# Revit family: Waste_Bin-Sotare-Magnuson_Group-
name_source: partatom
category: Furniture
revit_build: Autodesk Revit 2014 (Build: 20130308_1515(x64)
units: mm (PartAtom-declared; Revit-internal decimal feet)

## types (4) — shared parameters
Color/ Finish = Dark Anthracite. Anodized Silver. Luner White. Bronze Metallic.
Depth = 18"
Height = 33 3/4"
Manufacturer = Magnuson Group
Powder Coat Paint = MAG - Dark Anthracite
Type Comments = SOTARE
URL = www.magnusongroup.com
Width = 18"

## per-type parameters (varying)
| type | Center | Cost | Description | Full Body | Full Lid_Circle/Paper | Full Lid_Waste | Glide Finish | Left | Left Feet | Right | Right Feet |
| SO1809L-RIGHT | Yes | 1095 $ | Right side quarter elliptical shaped waste basket with internal rigid liner and removable wire bag ring. Includes one standard icon and adjustable glides. Capacity 14 gallons. | No | No | No | <By Category> | No | No | Yes | Yes |
| SO1809L-LEFT | Yes | 1095 $ | Left side quarter elliptical shaped waste receptacle with internal rigid liner and removable wire bag ring. Includes one standard icon and adjustable glides. Capacity 14 gallons. | No | No | No | MAG - Plastic Black | Yes | Yes | No | No |
| SO1818L | No | 1395 $ | Half elliptical shaped waste receptacle with internal rigid liner and removable wire bag ring. Single top opening. Includes two standard icons and adjustable glides. Capacity 34 gallons. | Yes | No | Yes | <By Category> | No | Yes | No | Yes |
| SO1818L-DBL | No | 1495 $ | Half elliptical shaped waste receptacle with internal rigid liner and removable wire bag ring. Double top opening. Includes two standard icons and adjustable glides. Capacity 34 gallons. | Yes | Yes | No | <By Category> | No | Yes | No | Yes |

note: column(s) folded — value = type name in every type: Model

## geometry (parser evidence)
native form markers: Sweep x3
no freeform markers — native parametric forms only
